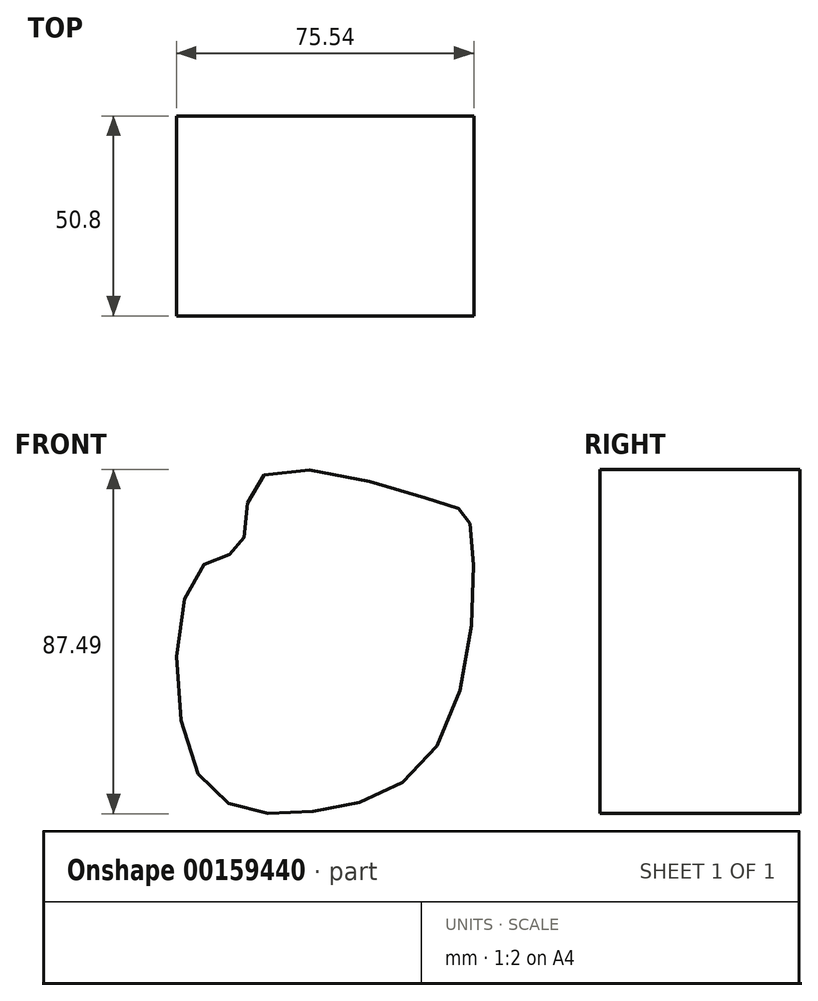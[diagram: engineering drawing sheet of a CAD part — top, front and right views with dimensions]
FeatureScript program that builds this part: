
annotation { "Feature Type Name" : "Feature", "Feature Type Description" : "" }
export const myFeature = defineFeature(function(context is Context, id is Id, definition is map)
    precondition{}
    {
        {
            var Q0;
            Q0=qCreatedBy(makeId("Front.planeOp"),FACE);
            var sketch = newSketch(context, id + "F0", { "sketchPlane" : qUnion([Q0])});
            skFitSpline(sketch, "E0", {"points": [v(-37.31, -29.06) * mm, v(-37.07, 23.08) * mm, v(-26.55, 28.58) * mm, v(-21.53, 46.28) * mm, v(25.6, 39.35) * mm, v(31.57, 34.8) * mm, v(24.16, -20.7) * mm, v(-10.29, -38.87) * mm, v(-37.31, -29.06) * mm]});
            skSolve(sketch);
        }
        {
            var Q0;
            Q0 = qSketchRegion(id + "F0", true);
            extrude(context, id + "F1", {"entities" : qUnion([Q0]), "depth" : 25.4 * mm, "hasSecondDirection" : true, "secondDirectionOppositeDirection" : true, "secondDirectionDepth" : 25.4 * mm});
        }
    });
